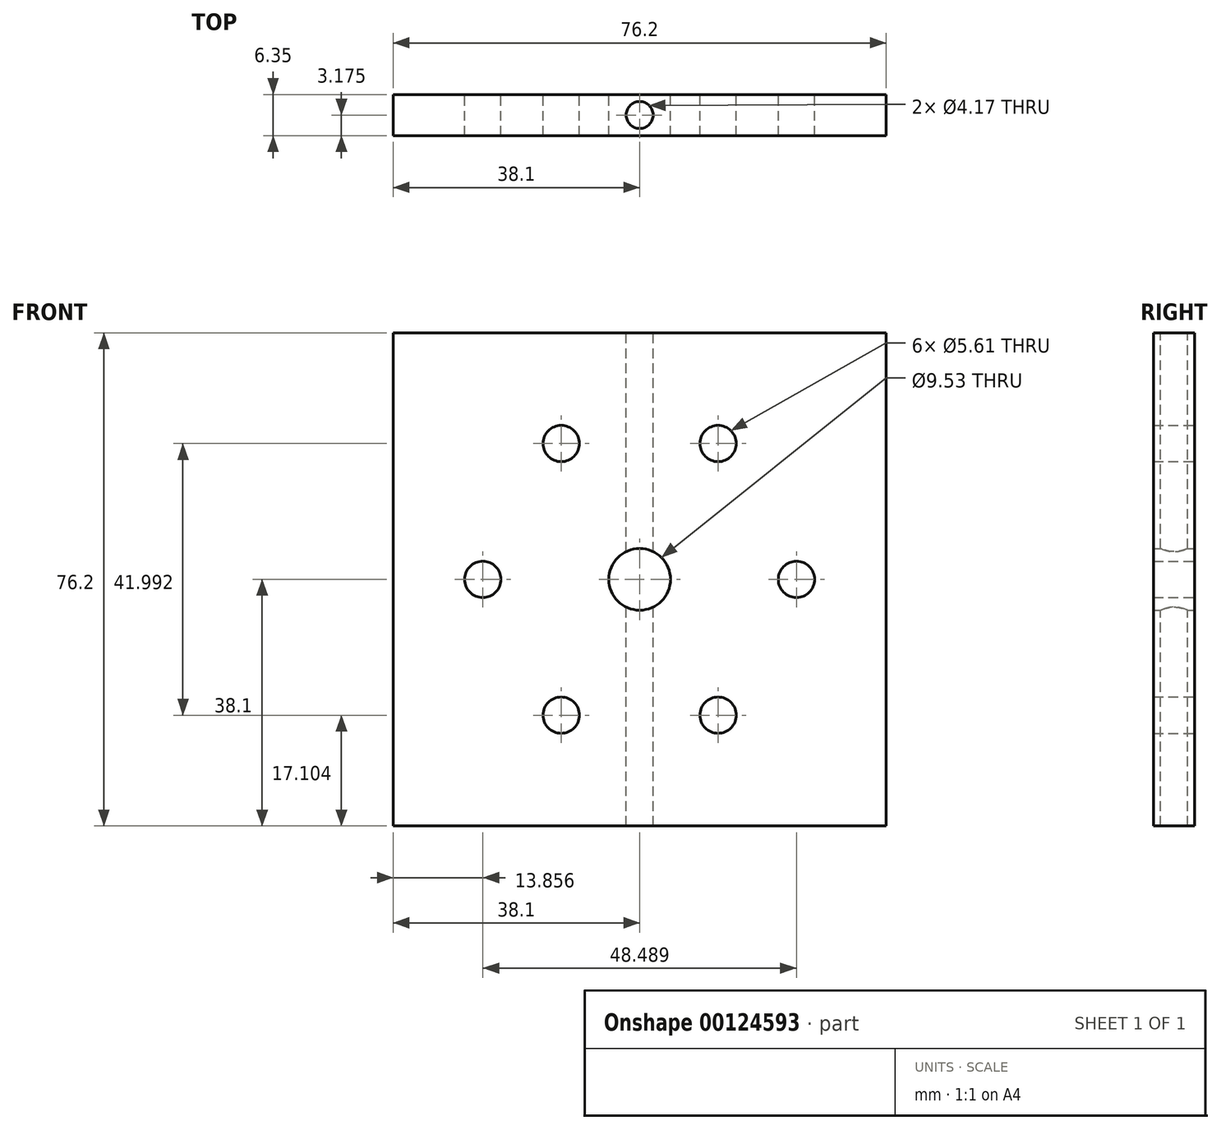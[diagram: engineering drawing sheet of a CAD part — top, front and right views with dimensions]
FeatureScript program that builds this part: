
annotation { "Feature Type Name" : "Feature", "Feature Type Description" : "" }
export const myFeature = defineFeature(function(context is Context, id is Id, definition is map)
    precondition{}
    {
        {
            var Q0;
            Q0=qCreatedBy(makeId("Front.planeOp"),FACE);
            var sketch = newSketch(context, id + "F0", { "sketchPlane" : qUnion([Q0])});
            skCircle(sketch, "E0", {"center": v(0, 0) * mm, "radius": 4.76 * mm});
            skLineSegment(sketch, "E1.bottom", {"start": v(38.1, -38.1) * mm, "end": v(-38.1, -38.1) * mm});
            skLineSegment(sketch, "E1.top", {"start": v(38.1, 38.1) * mm, "end": v(-38.1, 38.1) * mm});
            skLineSegment(sketch, "E1.left", {"start": v(38.1, -38.1) * mm, "end": v(38.1, 38.1) * mm});
            skLineSegment(sketch, "E1.right", {"start": v(-38.1, -38.1) * mm, "end": v(-38.1, 38.1) * mm});
            skLineSegment(sketch, "E2", {"start": v(0, -38.1) * mm, "end": v(0, 38.1) * mm, "construction": true});
            skLineSegment(sketch, "E3", {"start": v(-38.1, 0) * mm, "end": v(38.1, 0) * mm, "construction": true});
            skPoint(sketch, "E4", {"position": v(0, 27.05) * mm});
            skPoint(sketch, "E5", {"position": v(0, -27.05) * mm});
            skLineSegment(sketch, "E6", {"start": v(-38.1, -38.1) * mm, "end": v(38.1, 38.1) * mm, "construction": true});
            skLineSegment(sketch, "E7", {"start": v(38.1, -38.1) * mm, "end": v(-38.1, 38.1) * mm, "construction": true});
            skPoint(sketch, "E8", {"position": v(-19.13, 19.13) * mm});
            skPoint(sketch, "E9", {"position": v(19.13, 19.13) * mm});
            skPoint(sketch, "E10", {"position": v(27.05, 0) * mm});
            skPoint(sketch, "E11", {"position": v(-27.05, 0) * mm});
            skPoint(sketch, "E12", {"position": v(-17.75, -17.75) * mm});
            skPoint(sketch, "E13", {"position": v(19.13, -19.13) * mm});
            skCircle(sketch, "E14", {"center": v(0, 0) * mm, "radius": 27.05 * mm, "construction": true});
            skCircle(sketch, "E15", {"center": v(24.24, 0) * mm, "radius": 2.8 * mm});
            skCircle(sketch, "E16.1.0", {"center": v(12.12, 21) * mm, "radius": 2.8 * mm});
            skCircle(sketch, "E16.2.0", {"center": v(-12.12, 21) * mm, "radius": 2.8 * mm});
            skCircle(sketch, "E16.3.0", {"center": v(-24.24, 0) * mm, "radius": 2.8 * mm});
            skCircle(sketch, "E16.4.0", {"center": v(-12.12, -21) * mm, "radius": 2.8 * mm});
            skCircle(sketch, "E16.5.0", {"center": v(12.12, -21) * mm, "radius": 2.8 * mm});
            skSolve(sketch);
        }
        {
            var Q0;
            Q0=makeQuery(id+"F0.imprint","IMPRINT",FACE,{"disambiguationData":[TD([[makeQuery(id+"F0.imprint","IMPRINT",EDGE,{"derivedFrom":sQuery(id+"F0.wireOp",EDGE,"E0")}),-1.0]])]});
            extrude(context, id + "F1", {"entities" : qUnion([Q0]), "depth" : 6.35 * mm});
        }
        {
            var Q0;
            Q0=makeQuery(id+"F1.opExtrude","SWEPT_FACE",FACE,{"disambiguationData":[OSD([sQuery(id+"F0.wireOp",EDGE,"E1.top")])]});
            var sketch = newSketch(context, id + "F2", { "sketchPlane" : qUnion([Q0])});
            skLineSegment(sketch, "E17", {"start": v(0, -6.35) * mm, "end": v(0, 0) * mm, "construction": true});
            skCircle(sketch, "E18", {"center": v(0, -3.18) * mm, "radius": 2.08 * mm});
            skSolve(sketch);
        }
        {
            var Q0;
            Q0=makeQuery(id+"F2.imprint","IMPRINT",FACE,{"disambiguationData":[TD([[makeQuery(id+"F2.imprint","IMPRINT",EDGE,{"derivedFrom":sQuery(id+"F2.wireOp",EDGE,"E18")}),1.0]])]});
            extrude(context, id + "F3", {"entities" : qUnion([Q0]), "operationType" : NewBodyOperationType.REMOVE, "endBound" : BoundingType.THROUGH_ALL, "oppositeDirection" : true, "depth" : 25.4 * mm});
        }
    });
